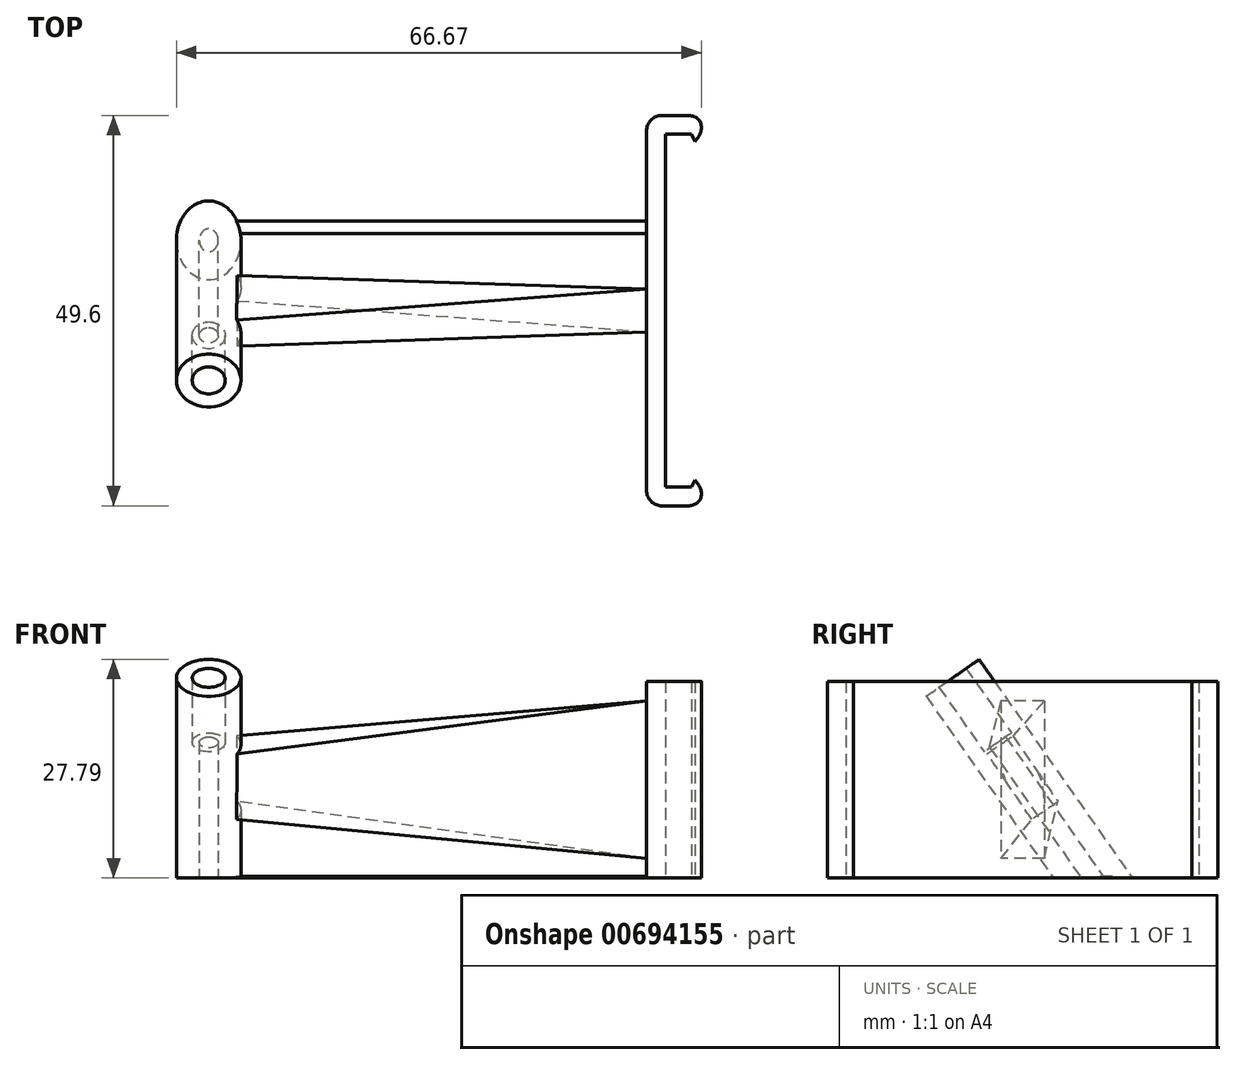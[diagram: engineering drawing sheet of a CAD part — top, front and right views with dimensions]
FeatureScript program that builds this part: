
annotation { "Feature Type Name" : "Feature", "Feature Type Description" : "" }
export const myFeature = defineFeature(function(context is Context, id is Id, definition is map)
    precondition{}
    {
        {
            var Q0;
            Q0=qCreatedBy(makeId("Top.planeOp"),FACE);
            var sketch = newSketch(context, id + "F0", { "sketchPlane" : qUnion([Q0])});
            skLineSegment(sketch, "E0", {"start": v(0, 0) * mm, "end": v(0, -22.4) * mm});
            skLineSegment(sketch, "E1", {"start": v(0, -22.4) * mm, "end": v(3.3, -22.4) * mm});
            skLineSegment(sketch, "E2", {"start": v(3.3, -22.4) * mm, "end": v(3.74, -21.5) * mm});
            skLineSegment(sketch, "E3.1", {"start": v(-0.4, -24.8) * mm, "end": v(2.84, -24.8) * mm});
            skLineSegment(sketch, "E3.2", {"start": v(-2.4, 0) * mm, "end": v(-2.4, -22.8) * mm});
            skLineSegment(sketch, "E4", {"start": v(3.74, -21.5) * mm, "end": v(4.25, -22.2) * mm});
            skPoint(sketch, "E5.visualSharp", {"position": v(-2.4, -24.8) * mm});
            skArc(sketch, "E5.filletArc", {"start": v(-2.4, -22.8) * mm, "mid": v(-1.81, -24.21) * mm, "end": v(-0.4, -24.8) * mm});
            skFitSpline(sketch, "E6", {"points": [v(4.25, -22.2) * mm, v(4.4, -24) * mm, v(2.84, -24.8) * mm], "startDerivative": vector(1.98, -2.67) * mm, "endDerivative": vector(-3.88, 0) * mm});
            skLineSegment(sketch, "E7.MirrorCS", {"start": v(3.74, 21.5) * mm, "end": v(4.25, 22.2) * mm});
            skLineSegment(sketch, "E8.MirrorCS", {"start": v(3.3, 22.4) * mm, "end": v(3.74, 21.5) * mm});
            skLineSegment(sketch, "E9.MirrorCS", {"start": v(-0.4, 24.8) * mm, "end": v(2.84, 24.8) * mm});
            skFitSpline(sketch, "E10.MirrorCS", {"points": [v(4.25, 22.2) * mm, v(4.4, 24) * mm, v(2.84, 24.8) * mm], "startDerivative": vector(1.98, 2.67) * mm, "endDerivative": vector(-3.88, 0) * mm});
            skLineSegment(sketch, "E11.MirrorCS", {"start": v(-2.4, 0) * mm, "end": v(-2.4, 22.8) * mm});
            skLineSegment(sketch, "E12.MirrorCS", {"start": v(0, 22.4) * mm, "end": v(3.3, 22.4) * mm});
            skLineSegment(sketch, "E13.MirrorCS", {"start": v(0, 0) * mm, "end": v(0, 22.4) * mm});
            skPoint(sketch, "E14.MirrorP", {"position": v(-2.4, 24.8) * mm});
            skArc(sketch, "E15.MirrorCS", {"start": v(-2.4, 22.8) * mm, "mid": v(-1.81, 24.21) * mm, "end": v(-0.4, 24.8) * mm});
            skSolve(sketch);
        }
        {
            var Q0;
            Q0=makeQuery(id+"F0.imprint","IMPRINT",FACE,{"disambiguationData":[TD([[makeQuery(id+"F0.imprint","IMPRINT",EDGE,{"derivedFrom":sQuery(id+"F0.wireOp",EDGE,"E0")}),-1.0]])]});
            extrude(context, id + "F1", {"entities" : qUnion([Q0]), "depth" : 25 * mm, "offsetDistance" : 25 * mm});
        }
        {
            var Q0;
            Q0=qCreatedBy(makeId("Right.planeOp"),FACE);
            cPlane(context, id + "F2", {"entities" : qUnion([Q0]), "cplaneType" : CPlaneType.OFFSET, "offset" : 55 * mm, "oppositeDirection" : true, "width" : 150 * mm, "height" : 150 * mm});
        }
        {
            var Q0;
            Q0=qCreatedBy(id+"F2.planeOp",FACE);
            var sketch = newSketch(context, id + "F3", { "sketchPlane" : qUnion([Q0])});
            skLineSegment(sketch, "E16.bottom", {"start": v(-1.23, 18) * mm, "end": v(-4.5, 15.71) * mm});
            skLineSegment(sketch, "E16.top", {"start": v(4.5, 9.81) * mm, "end": v(1.23, 7.52) * mm});
            skLineSegment(sketch, "E16.left", {"start": v(-1.23, 18) * mm, "end": v(4.5, 9.81) * mm});
            skLineSegment(sketch, "E16.right", {"start": v(-4.5, 15.71) * mm, "end": v(1.23, 7.52) * mm});
            skPoint(sketch, "E16.middle", {"position": v(0, 12.76) * mm});
            skLineSegment(sketch, "E17", {"start": v(2.87, 8.67) * mm, "end": v(-2.87, 16.86) * mm, "construction": true});
            skSolve(sketch);
        }
        {
            var Q0;
            Q0=makeQuery(id+"F1.opExtrude","SWEPT_FACE",FACE,{"disambiguationData":[OSD([sQuery(id+"F0.wireOp",EDGE,"E3.2"),sQuery(id+"F0.wireOp",EDGE,"E11.MirrorCS")])]});
            var sketch = newSketch(context, id + "F4", { "sketchPlane" : qUnion([Q0])});
            skLineSegment(sketch, "E18", {"start": v(0, 0) * mm, "end": v(0, 25) * mm, "construction": true});
            skLineSegment(sketch, "E19.bottom", {"start": v(-2.75, 22.5) * mm, "end": v(2.75, 22.5) * mm});
            skLineSegment(sketch, "E19.top", {"start": v(-2.75, 2.5) * mm, "end": v(2.75, 2.5) * mm});
            skLineSegment(sketch, "E19.left", {"start": v(-2.75, 22.5) * mm, "end": v(-2.75, 2.5) * mm});
            skLineSegment(sketch, "E19.right", {"start": v(2.75, 22.5) * mm, "end": v(2.75, 2.5) * mm});
            skPoint(sketch, "E19.middle", {"position": v(0, 12.5) * mm});
            skSolve(sketch);
        }
        {
            var Q1;
            Q1=makeQuery(id+"F4.imprint","IMPRINT",FACE,{"disambiguationData":[TD([[makeQuery(id+"F4.imprint","IMPRINT",EDGE,{"derivedFrom":sQuery(id+"F4.wireOp",EDGE,"E19.bottom")}),-1.0]])]});
            var Q2;
            Q2=makeQuery(id+"F3.imprint","IMPRINT",FACE,{"disambiguationData":[TD([[makeQuery(id+"F3.imprint","IMPRINT",EDGE,{"derivedFrom":sQuery(id+"F3.wireOp",EDGE,"E16.bottom")}),1.0]])]});
            loft(context, id + "F5", {"operationType" : NewBodyOperationType.ADD, "sheetProfilesArray" : [{ "sheetProfileEntities" : qUnion([Q1]) }, { "sheetProfileEntities" : qUnion([Q2]) }]});
        }
        {
            var Q0;
            Q0=makeQuery(id+"F5.opLoft","MID_CAP_EDGE",EDGE,{"disambiguationData":[OSD([sQuery(id+"F3.wireOp",EDGE,"E16.top"),sQuery(id+"F3.wireOp",EDGE,"E16.left"),sQuery(id+"F3.wireOp",EDGE,"E16.right")])],"capPos":1.0});
            cPlane(context, id + "F6", {"entities" : qUnion([Q0]), "cplaneType" : CPlaneType.MID_PLANE, "offset" : 25 * mm, "width" : 150 * mm, "height" : 150 * mm});
        }
        {
            var Q0;
            Q0=qCreatedBy(id+"F6.planeOp",FACE);
            var sketch = newSketch(context, id + "F7", { "sketchPlane" : qUnion([Q0])});
            skLineSegment(sketch, "E20", {"start": v(-58, 5.56) * mm, "end": v(-58, 15.8) * mm, "construction": true});
            skLineSegment(sketch, "E21", {"start": v(-59.2, 15.92) * mm, "end": v(-59.2, -9.08) * mm});
            skLineSegment(sketch, "E22", {"start": v(-59.2, -9.08) * mm, "end": v(-62.1, -9.08) * mm});
            skLineSegment(sketch, "E23", {"start": v(-62.1, -9.08) * mm, "end": v(-62.1, 25.92) * mm});
            skLineSegment(sketch, "E24", {"start": v(-62.1, 25.92) * mm, "end": v(-60.1, 25.92) * mm});
            skLineSegment(sketch, "E25", {"start": v(-60.1, 25.92) * mm, "end": v(-60.1, 15.92) * mm});
            skLineSegment(sketch, "E26", {"start": v(-60.1, 15.92) * mm, "end": v(-59.2, 15.92) * mm});
            skSolve(sketch);
        }
        {
            var Q0;
            Q0 = qSketchRegion(id + "F7", true);
            var Q1;
            Q1=sQuery(id+"F7.wireOp",EDGE,"E20");
            revolve(context, id + "F8", {"operationType" : NewBodyOperationType.ADD, "entities" : qUnion([Q0]), "axis" : qUnion([Q1]), "revolveType" : RevolveType.FULL});
        }
        {
            var Q0;
            Q0=qCreatedBy(makeId("Front.planeOp"),FACE);
            var sketch = newSketch(context, id + "F9", { "sketchPlane" : qUnion([Q0])});
            skLineSegment(sketch, "E27.bottom", {"start": v(-43.54, 0) * mm, "end": v(-70.96, 0) * mm});
            skLineSegment(sketch, "E27.top", {"start": v(-43.54, -9.75) * mm, "end": v(-70.96, -9.75) * mm});
            skLineSegment(sketch, "E27.left", {"start": v(-43.54, 0) * mm, "end": v(-43.54, -9.75) * mm});
            skLineSegment(sketch, "E27.right", {"start": v(-70.96, 0) * mm, "end": v(-70.96, -9.75) * mm});
            skSolve(sketch);
        }
        {
            var Q0;
            Q0=makeQuery(id+"F9.imprint","IMPRINT",FACE,{"disambiguationData":[TD([[makeQuery(id+"F9.imprint","IMPRINT",EDGE,{"derivedFrom":sQuery(id+"F9.wireOp",EDGE,"E27.bottom")}),1.0]])]});
            extrude(context, id + "F10", {"entities" : qUnion([Q0]), "operationType" : NewBodyOperationType.REMOVE, "oppositeDirection" : true, "depth" : 25 * mm, "offsetDistance" : 25 * mm});
        }
        {
            var Q0;
            Q0=makeQuery(id+"F1.opExtrude","SWEPT_FACE",FACE,{"disambiguationData":[OSD([sQuery(id+"F0.wireOp",EDGE,"E3.2"),sQuery(id+"F0.wireOp",EDGE,"E11.MirrorCS")])]});
            var sketch = newSketch(context, id + "F11", { "sketchPlane" : qUnion([Q0])});
            skLineSegment(sketch, "E28.bottom", {"start": v(-11.4, 0) * mm, "end": v(-9.8, 0) * mm});
            skLineSegment(sketch, "E28.top", {"start": v(-11.4, 0.2) * mm, "end": v(-9.8, 0.2) * mm});
            skLineSegment(sketch, "E28.left", {"start": v(-11.4, 0) * mm, "end": v(-11.4, 0.2) * mm});
            skLineSegment(sketch, "E28.right", {"start": v(-9.8, 0) * mm, "end": v(-9.8, 0.2) * mm});
            skSolve(sketch);
        }
        {
            var Q0;
            Q0=makeQuery(id+"F11.imprint","IMPRINT",FACE,{"disambiguationData":[TD([[makeQuery(id+"F11.imprint","IMPRINT",EDGE,{"derivedFrom":sQuery(id+"F11.wireOp",EDGE,"E28.bottom")}),-1.0]])]});
            extrude(context, id + "F12", {"entities" : qUnion([Q0]), "operationType" : NewBodyOperationType.ADD, "endBound" : BoundingType.UP_TO_NEXT, "depth" : 25 * mm, "offsetDistance" : 25 * mm});
        }
    });
